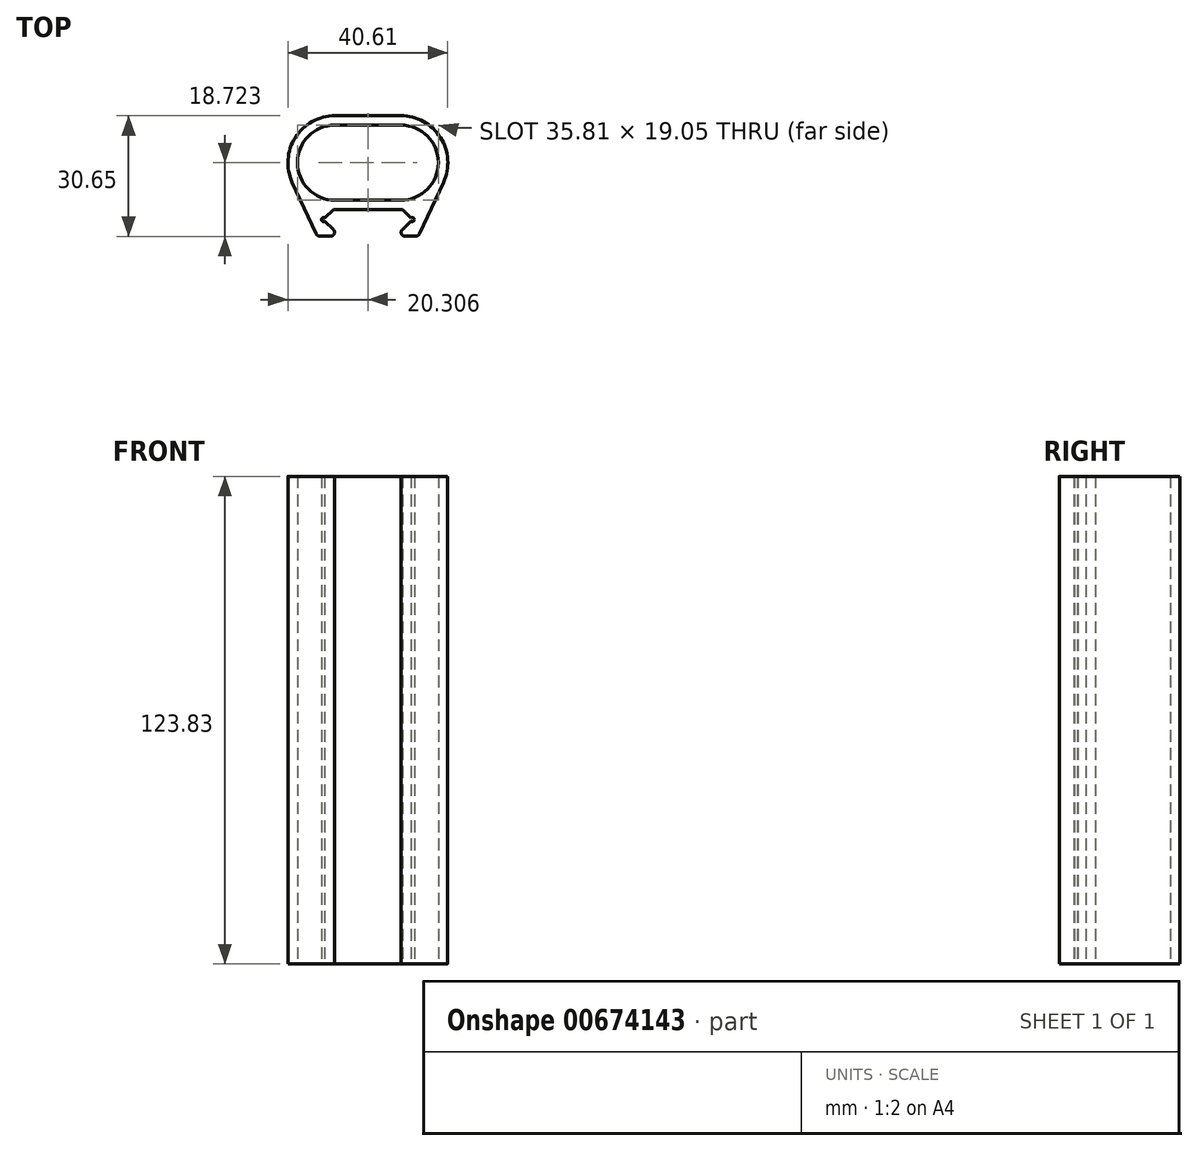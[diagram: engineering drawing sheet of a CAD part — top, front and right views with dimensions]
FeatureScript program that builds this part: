
annotation { "Feature Type Name" : "Feature", "Feature Type Description" : "" }
export const myFeature = defineFeature(function(context is Context, id is Id, definition is map)
    precondition{}
    {
        {
            var Q0;
            Q0=qCreatedBy(makeId("Top.planeOp"),FACE);
            var sketch = newSketch(context, id + "F0", { "sketchPlane" : qUnion([Q0])});
            skPoint(sketch, "E0.middle", {"position": v(0, 0.4) * mm});
            skLineSegment(sketch, "E1.top", {"start": v(-10.95, -13.58) * mm, "end": v(-8.76, -11.4) * mm});
            skLineSegment(sketch, "E1.left", {"start": v(-8.76, -16.48) * mm, "end": v(-10.95, -14.3) * mm});
            skLineSegment(sketch, "E2.top", {"start": v(8.77, -11.4) * mm, "end": v(10.96, -13.58) * mm});
            skLineSegment(sketch, "E2.right", {"start": v(8.76, -16.48) * mm, "end": v(10.96, -14.29) * mm});
            skArc(sketch, "E3", {"start": v(-10.95, -13.58) * mm, "mid": v(-11.8, -13.94) * mm, "end": v(-10.95, -14.3) * mm});
            skArc(sketch, "E4", {"start": v(10.96, -14.29) * mm, "mid": v(11.8, -13.93) * mm, "end": v(10.96, -13.58) * mm});
            skArc(sketch, "E5", {"start": v(-9.47, -18.19) * mm, "mid": v(-8.55, -17.57) * mm, "end": v(-8.76, -16.48) * mm});
            skArc(sketch, "E6", {"start": v(8.76, -16.48) * mm, "mid": v(8.55, -17.57) * mm, "end": v(9.47, -18.19) * mm});
            skLineSegment(sketch, "E7", {"start": v(-9.47, -18.19) * mm, "end": v(-12.03, -18.19) * mm});
            skLineSegment(sketch, "E8", {"start": v(9.47, -18.19) * mm, "end": v(12.03, -18.19) * mm});
            skPoint(sketch, "E9.1.start.orphan", {"position": v(-10.18, -17.9) * mm});
            skPoint(sketch, "E10.orphan", {"position": v(10.18, -17.9) * mm});
            skArc(sketch, "E11", {"start": v(12.03, -18.19) * mm, "mid": v(12.72, -17.99) * mm, "end": v(13.18, -17.45) * mm});
            skArc(sketch, "E12", {"start": v(-13.19, -17.45) * mm, "mid": v(-12.72, -17.99) * mm, "end": v(-12.03, -18.19) * mm});
            skArc(sketch, "E13", {"start": v(8.39, -9) * mm, "mid": v(17.91, 0.53) * mm, "end": v(8.39, 10.06) * mm});
            skLineSegment(sketch, "E14", {"start": v(-8.38, 10.06) * mm, "end": v(8.39, 10.06) * mm});
            skLineSegment(sketch, "E15", {"start": v(-8.38, -9) * mm, "end": v(8.39, -9) * mm});
            skArc(sketch, "E16.trimOffspring", {"start": v(-8.38, 10.06) * mm, "mid": v(-17.9, 0.53) * mm, "end": v(-8.38, -9) * mm});
            skArc(sketch, "E17.0", {"start": v(19.2, -4.49) * mm, "mid": v(18.44, 6.95) * mm, "end": v(8.39, 12.46) * mm});
            skArc(sketch, "E17.2", {"start": v(-8.38, 12.46) * mm, "mid": v(-18.43, 6.95) * mm, "end": v(-19.2, -4.48) * mm});
            skLineSegment(sketch, "E17.3", {"start": v(-8.38, 12.46) * mm, "end": v(8.39, 12.46) * mm});
            skLineSegment(sketch, "E18", {"start": v(-13.19, -17.45) * mm, "end": v(-19.2, -4.48) * mm});
            skLineSegment(sketch, "E19", {"start": v(13.18, -17.45) * mm, "end": v(19.2, -4.49) * mm});
            skLineSegment(sketch, "E20", {"start": v(-8.76, -11.4) * mm, "end": v(8.77, -11.4) * mm});
            skSolve(sketch);
        }
        {
            var Q0;
            Q0=makeQuery(id+"F0.imprint","IMPRINT",FACE,{"disambiguationData":[TD([[makeQuery(id+"F0.imprint","IMPRINT",EDGE,{"derivedFrom":sQuery(id+"F0.wireOp",EDGE,"E1.top")}),1.0]])]});
            extrude(context, id + "F1", {"entities" : qUnion([Q0]), "depth" : 123.82 * mm, "offsetDistance" : 25.4 * mm});
        }
    });
